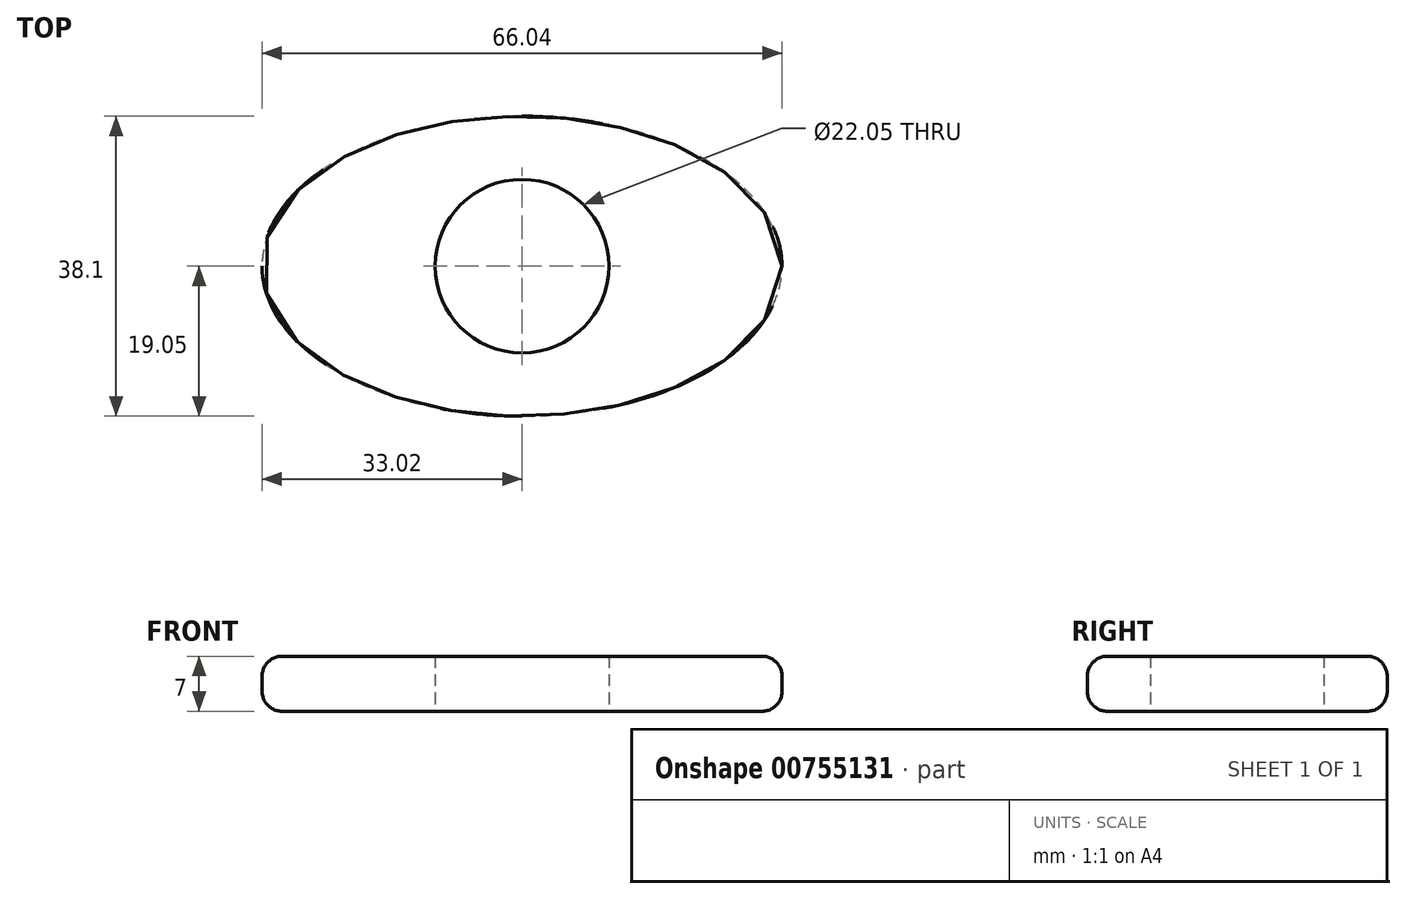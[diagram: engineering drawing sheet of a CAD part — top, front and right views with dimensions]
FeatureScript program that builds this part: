
annotation { "Feature Type Name" : "Feature", "Feature Type Description" : "" }
export const myFeature = defineFeature(function(context is Context, id is Id, definition is map)
    precondition{}
    {
        {
            var Q0;
            Q0=qCreatedBy(makeId("Top.planeOp"),FACE);
            var sketch = newSketch(context, id + "F0", { "sketchPlane" : qUnion([Q0])});
            skEllipse(sketch, "E0", {"center": v(0, 0) * mm, "majorRadius": 33.02 * mm, "minorRadius": 19.05 * mm, "majorAxis": v(1, 0)});
            skCircle(sketch, "E1", {"center": v(0, 0) * mm, "radius": 11.03 * mm});
            skLineSegment(sketch, "E2", {"start": v(-33.02, 0) * mm, "end": v(33.02, 0) * mm, "construction": true});
            skLineSegment(sketch, "E3", {"start": v(0, 19.05) * mm, "end": v(0, -19.05) * mm, "construction": true});
            skSolve(sketch);
        }
        {
            var Q0;
            Q0=makeQuery(id+"F0.imprint","IMPRINT",FACE,{"disambiguationData":[TD([[makeQuery(id+"F0.imprint","IMPRINT",EDGE,{"derivedFrom":sQuery(id+"F0.wireOp",EDGE,"E0")}),1.0]])]});
            extrude(context, id + "F1", {"entities" : qUnion([Q0]), "depth" : 7 * mm, "offsetDistance" : 25.4 * mm});
        }
        {
            var Q0;
            Q0=makeQuery(id+"F1.opExtrude","CAP_EDGE",EDGE,{"disambiguationData":[OSD([sQuery(id+"F0.wireOp",EDGE,"E0")])],"isStart":false});
            var Q1;
            Q1=makeQuery(id+"F1.opExtrude","CAP_EDGE",EDGE,{"disambiguationData":[OSD([sQuery(id+"F0.wireOp",EDGE,"E0")])],"isStart":true});
            fillet(context, id + "F2", {"entities" : qUnion([Q0, Q1]), "radius" : 2.54 * mm, "tangentPropagation" : true, "allowEdgeOverflow" : false});
        }
    });
